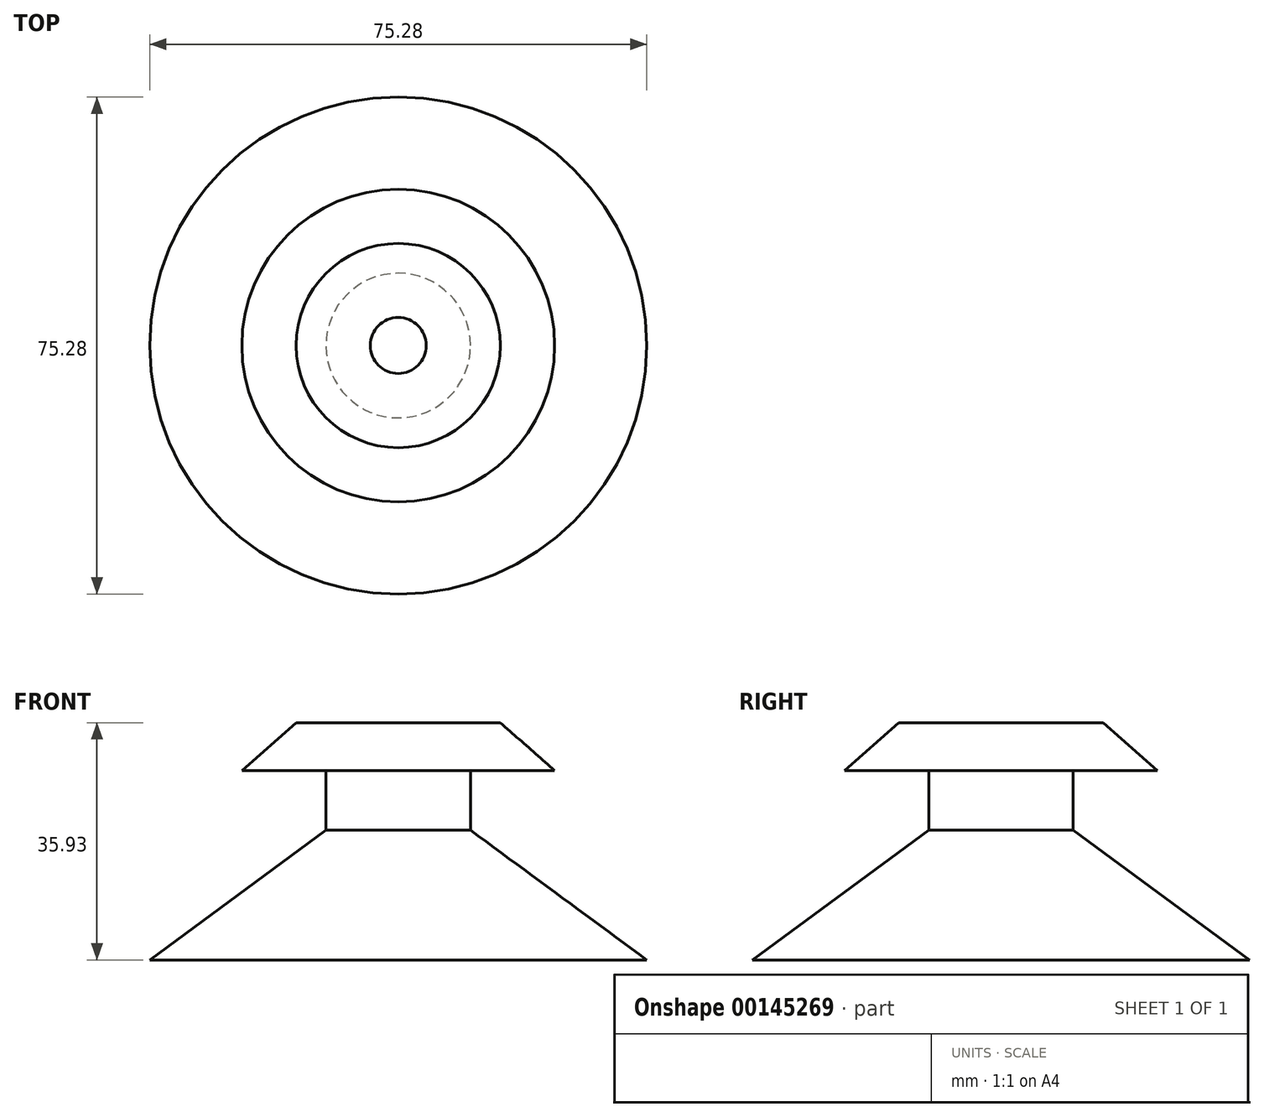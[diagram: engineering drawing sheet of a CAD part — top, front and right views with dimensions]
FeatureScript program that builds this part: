
annotation { "Feature Type Name" : "Feature", "Feature Type Description" : "" }
export const myFeature = defineFeature(function(context is Context, id is Id, definition is map)
    precondition{}
    {
        {
            var Q0;
            Q0=qCreatedBy(makeId("Front.planeOp"),FACE);
            var sketch = newSketch(context, id + "F0", { "sketchPlane" : qUnion([Q0])});
            skLineSegment(sketch, "E0", {"start": v(0, 0) * mm, "end": v(0, 35.93) * mm, "construction": true});
            skLineSegment(sketch, "E1", {"start": v(4.24, 35.93) * mm, "end": v(15.47, 35.93) * mm});
            skLineSegment(sketch, "E2", {"start": v(15.47, 35.93) * mm, "end": v(23.68, 28.68) * mm});
            skLineSegment(sketch, "E3", {"start": v(23.68, 28.68) * mm, "end": v(10.95, 28.68) * mm});
            skLineSegment(sketch, "E4", {"start": v(10.95, 28.68) * mm, "end": v(10.95, 19.64) * mm});
            skLineSegment(sketch, "E5", {"start": v(10.95, 19.64) * mm, "end": v(37.64, 0) * mm});
            skLineSegment(sketch, "E6.MirrorCS", {"start": v(-10.95, 28.68) * mm, "end": v(-10.95, 19.64) * mm});
            skLineSegment(sketch, "E7.MirrorCS", {"start": v(-15.47, 35.93) * mm, "end": v(-23.68, 28.68) * mm});
            skLineSegment(sketch, "E8.MirrorCS", {"start": v(-23.68, 28.68) * mm, "end": v(-10.95, 28.68) * mm});
            skLineSegment(sketch, "E9.MirrorCS", {"start": v(-4.24, 35.93) * mm, "end": v(-15.47, 35.93) * mm});
            skLineSegment(sketch, "E10.MirrorCS", {"start": v(-10.95, 19.64) * mm, "end": v(-37.64, 0) * mm});
            skSolve(sketch);
        }
        {
            var Q0;
            Q0=sQuery(id+"F0.wireOp",EDGE,"E9.MirrorCS");
            var Q1;
            Q1=sQuery(id+"F0.wireOp",EDGE,"E7.MirrorCS");
            var Q2;
            Q2=sQuery(id+"F0.wireOp",EDGE,"E8.MirrorCS");
            var Q3;
            Q3=sQuery(id+"F0.wireOp",EDGE,"E6.MirrorCS");
            var Q4;
            Q4=sQuery(id+"F0.wireOp",EDGE,"E10.MirrorCS");
            var Q5;
            Q5=sQuery(id+"F0.wireOp",EDGE,"E0");
            revolve(context, id + "F1", {"bodyType" : ToolBodyType.SURFACE, "surfaceEntities" : qUnion([Q0, Q1, Q2, Q3, Q4]), "axis" : qUnion([Q5]), "revolveType" : RevolveType.FULL});
        }
    });
